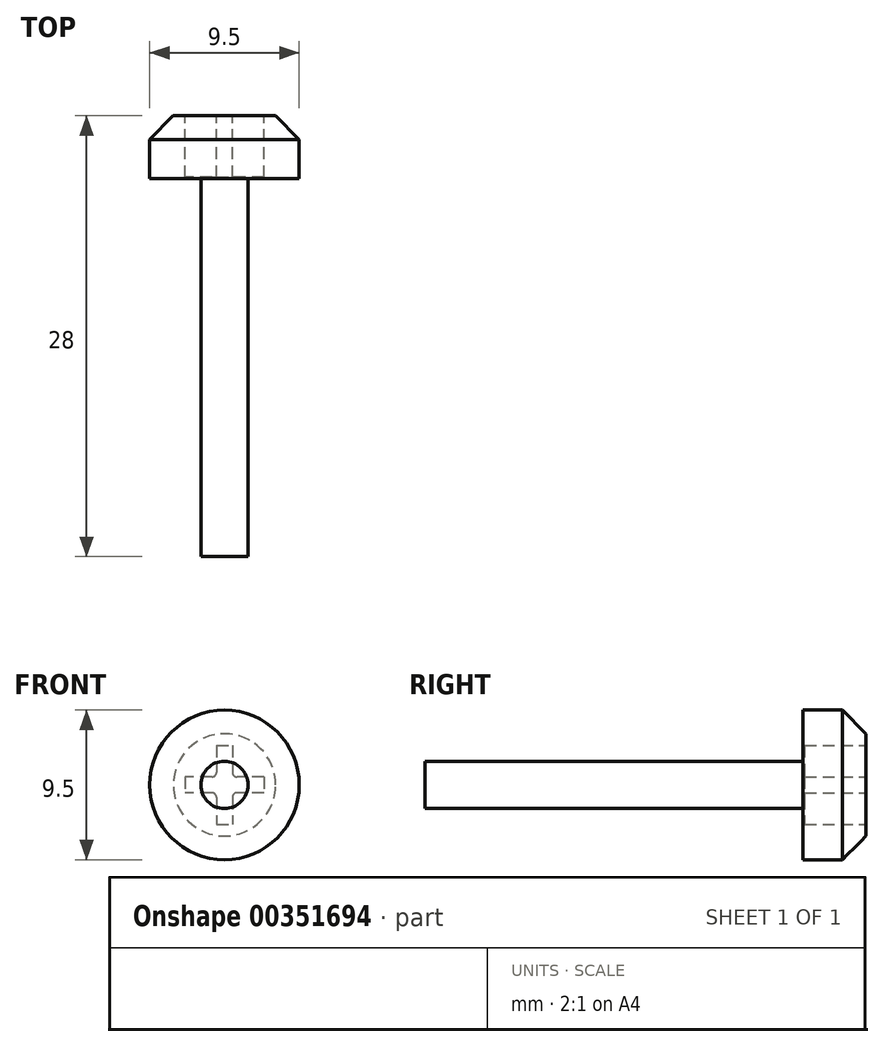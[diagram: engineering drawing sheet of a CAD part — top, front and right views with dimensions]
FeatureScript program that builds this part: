
annotation { "Feature Type Name" : "Feature", "Feature Type Description" : "" }
export const myFeature = defineFeature(function(context is Context, id is Id, definition is map)
    precondition{}
    {
        {
            var Q0;
            Q0=qCreatedBy(makeId("Front.planeOp"),FACE);
            var sketch = newSketch(context, id + "F0", { "sketchPlane" : qUnion([Q0])});
            skCircle(sketch, "E0", {"center": v(0, 0) * mm, "radius": 1.5 * mm});
            skSolve(sketch);
        }
        {
            var Q0;
            Q0 = qSketchRegion(id + "F0", true);
            extrude(context, id + "F1", {"entities" : qUnion([Q0]), "endBound" : BoundingType.SYMMETRIC, "depth" : 24 * mm});
        }
        {
            var Q0;
            Q0=makeQuery(id+"F1.opExtrude","CAP_FACE",FACE,{"disambiguationData":[OSD([sQuery(id+"F0.wireOp",EDGE,"E0")])],"isStart":true});
            var sketch = newSketch(context, id + "F2", { "sketchPlane" : qUnion([Q0])});
            skCircle(sketch, "E1", {"center": v(0, 0) * mm, "radius": 4.75 * mm});
            skSolve(sketch);
        }
        {
            var Q0;
            Q0=makeQuery(id+"F2.imprint","IMPRINT",FACE,{"disambiguationData":[TD([[makeQuery(id+"F2.imprint","IMPRINT",EDGE,{"derivedFrom":sQuery(id+"F2.wireOp",EDGE,"E1")}),1.0]])]});
            var Q1;
            Q1=makeQuery(id+"F2.imprint","IMPRINT",FACE,{"disambiguationData":[TD([[makeQuery(id+"F2.imprint","IMPRINT",EDGE,{"derivedFrom":makeQuery(id+"F1.opExtrude","CAP_EDGE",EDGE,{"disambiguationData":[OSD([sQuery(id+"F0.wireOp",EDGE,"E0")])],"isStart":true})}),-1.0]])]});
            extrude(context, id + "F3", {"entities" : qUnion([Q0, Q1]), "operationType" : NewBodyOperationType.ADD, "depth" : 2.5 * mm});
        }
        {
            var Q0;
            Q0=qCreatedBy(makeId("Front.planeOp"),FACE);
            cPlane(context, id + "F4", {"entities" : qUnion([Q0]), "cplaneType" : CPlaneType.OFFSET, "offset" : 16 * mm, "oppositeDirection" : true, "width" : 152.4 * mm, "height" : 152.4 * mm});
        }
        {
            var Q0;
            Q0=qCreatedBy(id+"F4.planeOp",FACE);
            var sketch = newSketch(context, id + "F5", { "sketchPlane" : qUnion([Q0])});
            skCircle(sketch, "E2", {"center": v(0, 0) * mm, "radius": 3.25 * mm});
            skSolve(sketch);
        }
        {
            var Q1;
            Q1=makeQuery(id+"F5.imprint","IMPRINT",FACE,{"disambiguationData":[TD([[makeQuery(id+"F5.imprint","IMPRINT",EDGE,{"derivedFrom":sQuery(id+"F5.wireOp",EDGE,"E2")}),1.0]])]});
            var Q2;
            Q2=makeQuery(id+"F3.opExtrude","CAP_FACE",FACE,{"disambiguationData":[OSD([sQuery(id+"F2.wireOp",EDGE,"E1")])],"isStart":false});
            loft(context, id + "F6", {"operationType" : NewBodyOperationType.ADD, "sheetProfilesArray" : [{ "sheetProfileEntities" : qUnion([Q1]) }, { "sheetProfileEntities" : qUnion([Q2]) }]});
        }
        {
            var Q0;
            Q0=makeQuery(id+"F6.opLoft","CAP_FACE",FACE,{"disambiguationData":[OSD([makeQuery(id+"F5.imprint","IMPRINT",FACE,{"disambiguationData":[TD([[makeQuery(id+"F5.imprint","IMPRINT",EDGE,{"derivedFrom":sQuery(id+"F5.wireOp",EDGE,"E2")}),1.0]])]})])],"isStart":true});
            var sketch = newSketch(context, id + "F7", { "sketchPlane" : qUnion([Q0])});
            skLineSegment(sketch, "E3.bottom", {"start": v(-2.5, 0.5) * mm, "end": v(2.5, 0.5) * mm});
            skLineSegment(sketch, "E3.top", {"start": v(-2.5, -0.5) * mm, "end": v(2.5, -0.5) * mm});
            skLineSegment(sketch, "E3.left", {"start": v(-2.5, 0.5) * mm, "end": v(-2.5, -0.5) * mm});
            skLineSegment(sketch, "E3.right", {"start": v(2.5, 0.5) * mm, "end": v(2.5, -0.5) * mm});
            skPoint(sketch, "E3.middle", {"position": v(0, 0) * mm});
            skLineSegment(sketch, "E4.bottom", {"start": v(0.5, 2.5) * mm, "end": v(-0.5, 2.5) * mm});
            skLineSegment(sketch, "E4.top", {"start": v(0.5, -2.5) * mm, "end": v(-0.5, -2.5) * mm});
            skLineSegment(sketch, "E4.left", {"start": v(0.5, 2.5) * mm, "end": v(0.5, -2.5) * mm});
            skLineSegment(sketch, "E4.right", {"start": v(-0.5, 2.5) * mm, "end": v(-0.5, -2.5) * mm});
            skSolve(sketch);
        }
        {
            var Q0;
            {var subQ5=sQuery(id+"F7.wireOp",EDGE,"E4.top");Q0=makeQuery(id+"F7.imprint","IMPRINT",FACE,{"disambiguationData":[TD([[makeQuery(id+"F7.imprint","IMPRINT",EDGE,{"derivedFrom":subQ5}),-1.0]])]});}
            var Q1;
            {var subQ0=sQuery(id+"F7.wireOp",EDGE,"E4.right");var subQ1=sQuery(id+"F7.wireOp",EDGE,"E3.bottom");var subQ2=makeQuery(id+"F7.imprint","INTERSECT",VERTEX,{"derivedFrom":[subQ1,subQ0]});Q1=makeQuery(id+"F7.imprint","IMPRINT",FACE,{"disambiguationData":[TD([[makeQuery(id+"F7.imprint","IMPRINT",EDGE,{"disambiguationData":[TD([[subQ2,-1.0]])],"derivedFrom":subQ1}),-1.0]])]});}
            var Q2;
            {var subQ0=sQuery(id+"F7.wireOp",EDGE,"E3.left");Q2=makeQuery(id+"F7.imprint","IMPRINT",FACE,{"disambiguationData":[TD([[makeQuery(id+"F7.imprint","IMPRINT",EDGE,{"derivedFrom":subQ0}),1.0]])]});}
            var Q3;
            {var subQ5=sQuery(id+"F7.wireOp",EDGE,"E4.bottom");Q3=makeQuery(id+"F7.imprint","IMPRINT",FACE,{"disambiguationData":[TD([[makeQuery(id+"F7.imprint","IMPRINT",EDGE,{"derivedFrom":subQ5}),1.0]])]});}
            var Q4;
            {var subQ0=sQuery(id+"F7.wireOp",EDGE,"E3.right");Q4=makeQuery(id+"F7.imprint","IMPRINT",FACE,{"disambiguationData":[TD([[makeQuery(id+"F7.imprint","IMPRINT",EDGE,{"derivedFrom":subQ0}),-1.0]])]});}
            extrude(context, id + "F8", {"entities" : qUnion([Q0, Q1, Q2, Q3, Q4]), "operationType" : NewBodyOperationType.REMOVE, "oppositeDirection" : true, "depth" : 3.9 * mm});
        }
        {
            var Q0;
            Q0=makeQuery(id+"F8.boolean.opBoolean","COPY",EDGE,{"derivedFrom":makeQuery(id+"F8.opExtrude","SWEPT_EDGE",EDGE,{"disambiguationData":[OSD([sQuery(id+"F7.wireOp",EDGE,"E3.bottom"),sQuery(id+"F7.wireOp",EDGE,"E4.left")])]})});
            var Q1;
            Q1=makeQuery(id+"F8.boolean.opBoolean","COPY",EDGE,{"derivedFrom":makeQuery(id+"F8.opExtrude","SWEPT_EDGE",EDGE,{"disambiguationData":[OSD([sQuery(id+"F7.wireOp",EDGE,"E3.bottom"),sQuery(id+"F7.wireOp",EDGE,"E4.right")])]})});
            var Q2;
            Q2=makeQuery(id+"F8.boolean.opBoolean","COPY",EDGE,{"derivedFrom":makeQuery(id+"F8.opExtrude","SWEPT_EDGE",EDGE,{"disambiguationData":[OSD([sQuery(id+"F7.wireOp",EDGE,"E3.top"),sQuery(id+"F7.wireOp",EDGE,"E4.right")])]})});
            var Q3;
            Q3=makeQuery(id+"F8.boolean.opBoolean","COPY",EDGE,{"derivedFrom":makeQuery(id+"F8.opExtrude","SWEPT_EDGE",EDGE,{"disambiguationData":[OSD([sQuery(id+"F7.wireOp",EDGE,"E3.top"),sQuery(id+"F7.wireOp",EDGE,"E4.left")])]})});
            fillet(context, id + "F9", {"entities" : qUnion([Q0, Q1, Q2, Q3]), "radius" : 0.3 * mm, "tangentPropagation" : true, "allowEdgeOverflow" : false});
        }
    });
